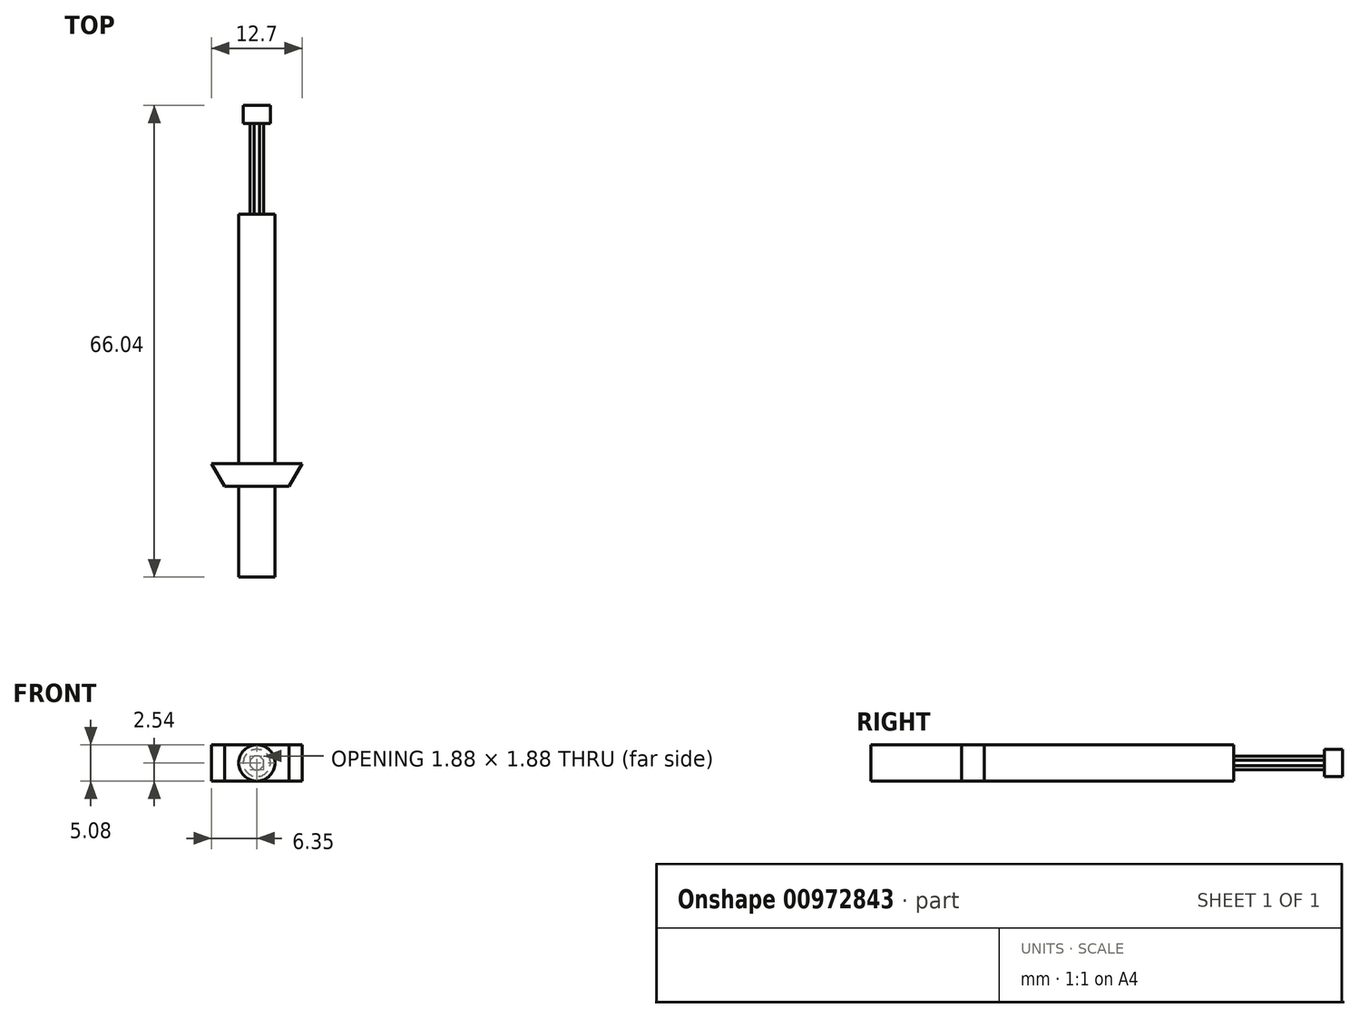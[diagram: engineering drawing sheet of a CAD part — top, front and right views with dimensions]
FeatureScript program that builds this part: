
annotation { "Feature Type Name" : "Feature", "Feature Type Description" : "" }
export const myFeature = defineFeature(function(context is Context, id is Id, definition is map)
    precondition{}
    {
        {
            var Q0;
            Q0=qCreatedBy(makeId("Front.planeOp"),FACE);
            var sketch = newSketch(context, id + "F0", { "sketchPlane" : qUnion([Q0])});
            skCircle(sketch, "E0", {"center": v(0, 0) * mm, "radius": 2.54 * mm});
            skSolve(sketch);
        }
        {
            var Q0;
            Q0=makeQuery(id+"F0.imprint","IMPRINT",FACE,{"disambiguationData":[TD([[makeQuery(id+"F0.imprint","IMPRINT",EDGE,{"derivedFrom":sQuery(id+"F0.wireOp",EDGE,"E0")}),1.0]])]});
            extrude(context, id + "F1", {"entities" : qUnion([Q0]), "depth" : 38.1 * mm, "offsetDistance" : 25.4 * mm});
        }
        {
            var Q0;
            Q0=makeQuery(id+"F1.opExtrude","CAP_FACE",FACE,{"disambiguationData":[OSD([sQuery(id+"F0.wireOp",EDGE,"E0")])],"isStart":true});
            var sketch = newSketch(context, id + "F2", { "sketchPlane" : qUnion([Q0])});
            skLineSegment(sketch, "E1.0", {"start": v(-0.39, 0.94) * mm, "end": v(0.39, 0.94) * mm});
            skLineSegment(sketch, "E1.1", {"start": v(0.39, 0.94) * mm, "end": v(0.94, 0.39) * mm});
            skLineSegment(sketch, "E1.2", {"start": v(0.94, 0.39) * mm, "end": v(0.94, -0.39) * mm});
            skLineSegment(sketch, "E1.3", {"start": v(0.94, -0.39) * mm, "end": v(0.39, -0.94) * mm});
            skLineSegment(sketch, "E1.4", {"start": v(0.39, -0.94) * mm, "end": v(-0.39, -0.94) * mm});
            skLineSegment(sketch, "E1.5", {"start": v(-0.39, -0.94) * mm, "end": v(-0.94, -0.39) * mm});
            skLineSegment(sketch, "E1.6", {"start": v(-0.94, -0.39) * mm, "end": v(-0.94, 0.39) * mm});
            skLineSegment(sketch, "E1.7", {"start": v(-0.94, 0.39) * mm, "end": v(-0.39, 0.94) * mm});
            skPoint(sketch, "E1.0.midPoint", {"position": v(0, 0.94) * mm});
            skSolve(sketch);
        }
        {
            var Q0;
            Q0=makeQuery(id+"F2.imprint","IMPRINT",FACE,{"disambiguationData":[TD([[makeQuery(id+"F2.imprint","IMPRINT",EDGE,{"derivedFrom":sQuery(id+"F2.wireOp",EDGE,"E1.0")}),-1.0]])]});
            extrude(context, id + "F3", {"entities" : qUnion([Q0]), "operationType" : NewBodyOperationType.ADD, "depth" : 12.7 * mm, "offsetDistance" : 25.4 * mm});
        }
        {
            var Q0;
            Q0=makeQuery(id+"F3.opExtrude","CAP_FACE",FACE,{"disambiguationData":[OSD([sQuery(id+"F2.wireOp",EDGE,"E1.0"),sQuery(id+"F2.wireOp",EDGE,"E1.1"),sQuery(id+"F2.wireOp",EDGE,"E1.2"),sQuery(id+"F2.wireOp",EDGE,"E1.3"),sQuery(id+"F2.wireOp",EDGE,"E1.4"),sQuery(id+"F2.wireOp",EDGE,"E1.5"),sQuery(id+"F2.wireOp",EDGE,"E1.6"),sQuery(id+"F2.wireOp",EDGE,"E1.7")])],"isStart":false});
            var sketch = newSketch(context, id + "F4", { "sketchPlane" : qUnion([Q0])});
            skCircle(sketch, "E2", {"center": v(0, 0) * mm, "radius": 1.9 * mm});
            skSolve(sketch);
        }
        {
            var Q0;
            Q0=makeQuery(id+"F4.imprint","IMPRINT",FACE,{"disambiguationData":[TD([[makeQuery(id+"F4.imprint","IMPRINT",EDGE,{"derivedFrom":sQuery(id+"F4.wireOp",EDGE,"E2")}),1.0]])]});
            var Q1;
            Q1=makeQuery(id+"F4.imprint","IMPRINT",FACE,{"disambiguationData":[TD([[makeQuery(id+"F4.imprint","IMPRINT",EDGE,{"derivedFrom":makeQuery(id+"F3.opExtrude","CAP_EDGE",EDGE,{"disambiguationData":[OSD([sQuery(id+"F2.wireOp",EDGE,"E1.0")])],"isStart":false})}),-1.0]])]});
            extrude(context, id + "F5", {"entities" : qUnion([Q0, Q1]), "operationType" : NewBodyOperationType.ADD, "depth" : 2.54 * mm, "offsetDistance" : 25.4 * mm});
        }
        {
            var Q0;
            Q0=qCreatedBy(makeId("Top.planeOp"),FACE);
            var sketch = newSketch(context, id + "F6", { "sketchPlane" : qUnion([Q0])});
            skLineSegment(sketch, "E3", {"start": v(0, 0) * mm, "end": v(0, -34.93) * mm});
            skLineSegment(sketch, "E4", {"start": v(0, -34.93) * mm, "end": v(-6.35, -34.93) * mm});
            skLineSegment(sketch, "E5", {"start": v(0, -34.93) * mm, "end": v(6.35, -34.93) * mm});
            skLineSegment(sketch, "E6", {"start": v(6.35, -34.92) * mm, "end": v(4.52, -38.1) * mm});
            skLineSegment(sketch, "E7", {"start": v(-6.35, -34.93) * mm, "end": v(-4.52, -38.1) * mm});
            skLineSegment(sketch, "E8", {"start": v(-4.52, -38.1) * mm, "end": v(4.52, -38.1) * mm});
            skLineSegment(sketch, "E9", {"start": v(0, -34.93) * mm, "end": v(0, -38.1) * mm});
            skSolve(sketch);
        }
        {
            var Q0;
            Q0=makeQuery(id+"F6.imprint","IMPRINT",FACE,{"disambiguationData":[TD([[makeQuery(id+"F6.imprint","IMPRINT",EDGE,{"derivedFrom":sQuery(id+"F6.wireOp",EDGE,"E4")}),1.0]])]});
            var Q1;
            Q1=makeQuery(id+"F6.imprint","IMPRINT",FACE,{"disambiguationData":[TD([[makeQuery(id+"F6.imprint","IMPRINT",EDGE,{"derivedFrom":sQuery(id+"F6.wireOp",EDGE,"E5")}),-1.0]])]});
            extrude(context, id + "F7", {"entities" : qUnion([Q0, Q1]), "operationType" : NewBodyOperationType.ADD, "endBound" : BoundingType.SYMMETRIC, "depth" : 5.08 * mm, "offsetDistance" : 25.4 * mm});
        }
        {
            var Q0;
            Q0=makeQuery(id+"F7.opExtrude","SWEPT_FACE",FACE,{"disambiguationData":[OSD([sQuery(id+"F6.wireOp",EDGE,"E8")])]});
            var sketch = newSketch(context, id + "F8", { "sketchPlane" : qUnion([Q0])});
            skCircle(sketch, "E10", {"center": v(0, 0) * mm, "radius": 2.54 * mm});
            skSolve(sketch);
        }
        {
            var Q0;
            {var subQ0=sQuery(id+"F8.wireOp",EDGE,"E10");var subQ1=sQuery(id+"F6.wireOp",EDGE,"E8");var subQ2=makeQuery(id+"F8.imprint","INTERSECT",VERTEX,{"derivedFrom":[makeQuery(id+"F7.opExtrude","CAP_EDGE",EDGE,{"disambiguationData":[OSD([subQ1])],"isStart":true}),subQ0]});Q0=makeQuery(id+"F8.imprint","IMPRINT",FACE,{"disambiguationData":[TD([[makeQuery(id+"F8.imprint","IMPRINT",EDGE,{"disambiguationData":[TD([[subQ2,1.0]])],"derivedFrom":subQ0}),1.0]])]});}
            extrude(context, id + "F9", {"entities" : qUnion([Q0]), "operationType" : NewBodyOperationType.ADD, "depth" : 12.7 * mm, "offsetDistance" : 25.4 * mm});
        }
    });
